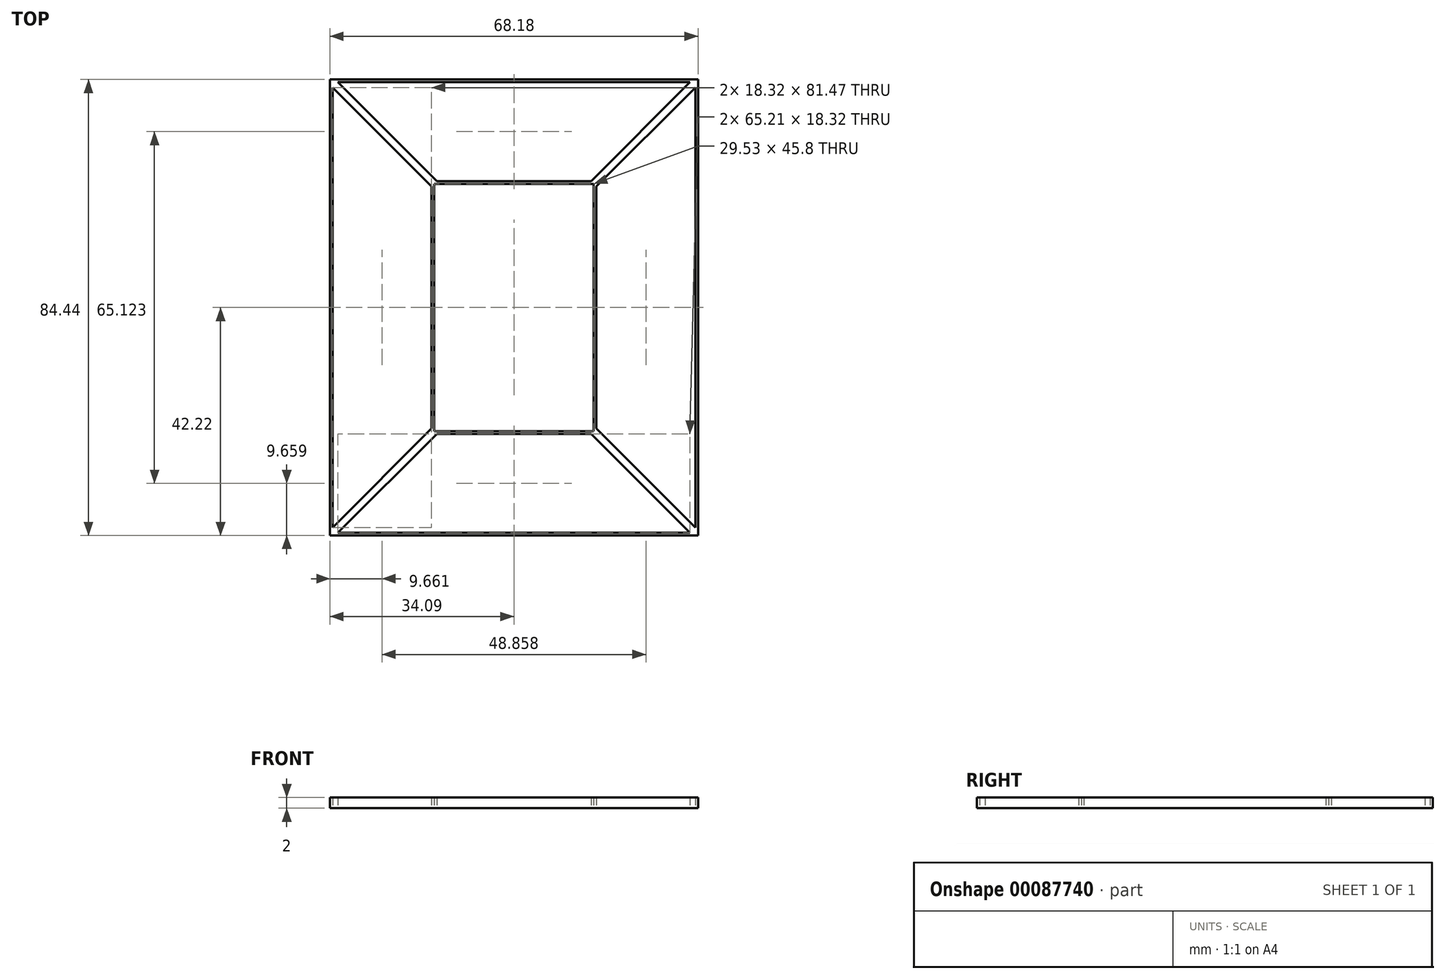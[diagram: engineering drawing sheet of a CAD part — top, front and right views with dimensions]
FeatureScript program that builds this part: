
annotation { "Feature Type Name" : "Feature", "Feature Type Description" : "" }
export const myFeature = defineFeature(function(context is Context, id is Id, definition is map)
    precondition{}
    {
        {
            var Q0;
            Q0=qCreatedBy(makeId("Top.planeOp"),FACE);
            var sketch = newSketch(context, id + "F0", { "sketchPlane" : qUnion([Q0])});
            skLineSegment(sketch, "E0", {"start": v(-33.6, 41.72) * mm, "end": v(-33.6, -41.72) * mm});
            skLineSegment(sketch, "E1", {"start": v(-33.6, -41.72) * mm, "end": v(33.6, -41.72) * mm});
            skLineSegment(sketch, "E2", {"start": v(33.6, -41.72) * mm, "end": v(33.6, 41.72) * mm});
            skLineSegment(sketch, "E3", {"start": v(33.6, 41.72) * mm, "end": v(-33.6, 41.72) * mm});
            skLineSegment(sketch, "E4.0", {"start": v(34.1, 42.22) * mm, "end": v(-34.1, 42.22) * mm});
            skLineSegment(sketch, "E4.1", {"start": v(34.1, -42.22) * mm, "end": v(34.1, 42.22) * mm});
            skLineSegment(sketch, "E4.2", {"start": v(-34.1, -42.22) * mm, "end": v(34.1, -42.22) * mm});
            skLineSegment(sketch, "E4.3", {"start": v(-34.1, 42.22) * mm, "end": v(-34.1, -42.22) * mm});
            skLineSegment(sketch, "E5.bottom", {"start": v(-14.77, 22.9) * mm, "end": v(14.77, 22.9) * mm});
            skLineSegment(sketch, "E5.top", {"start": v(-14.77, -22.9) * mm, "end": v(14.77, -22.9) * mm});
            skLineSegment(sketch, "E5.left", {"start": v(-14.77, 22.9) * mm, "end": v(-14.77, -22.9) * mm});
            skLineSegment(sketch, "E5.right", {"start": v(14.77, 22.9) * mm, "end": v(14.77, -22.9) * mm});
            skLineSegment(sketch, "E6.0", {"start": v(-15.27, 23.4) * mm, "end": v(15.27, 23.4) * mm});
            skLineSegment(sketch, "E6.1", {"start": v(-15.27, 23.4) * mm, "end": v(-15.27, -23.4) * mm});
            skLineSegment(sketch, "E6.2", {"start": v(-15.27, -23.4) * mm, "end": v(15.27, -23.4) * mm});
            skLineSegment(sketch, "E6.3", {"start": v(15.27, 23.4) * mm, "end": v(15.27, -23.4) * mm});
            skLineSegment(sketch, "E7", {"start": v(-32.6, -41.72) * mm, "end": v(-14.28, -23.4) * mm});
            skLineSegment(sketch, "E8", {"start": v(-33.6, -41.72) * mm, "end": v(-15.27, -23.4) * mm, "construction": true});
            skLineSegment(sketch, "E9.MirrorCS", {"start": v(-33.6, -40.74) * mm, "end": v(-15.27, -22.41) * mm});
            skLineSegment(sketch, "E10", {"start": v(0, -42.22) * mm, "end": v(0, 34.98) * mm, "construction": true});
            skLineSegment(sketch, "E11", {"start": v(-33.6, 0) * mm, "end": v(33.6, 0) * mm, "construction": true});
            skLineSegment(sketch, "E12.MirrorCS", {"start": v(-33.6, 40.74) * mm, "end": v(-15.27, 22.41) * mm});
            skLineSegment(sketch, "E13.MirrorCS", {"start": v(-32.6, 41.72) * mm, "end": v(-14.28, 23.4) * mm});
            skLineSegment(sketch, "E14.MirrorCS", {"start": v(33.6, 40.74) * mm, "end": v(15.27, 22.41) * mm});
            skLineSegment(sketch, "E15.MirrorCS", {"start": v(32.6, 41.72) * mm, "end": v(14.28, 23.4) * mm});
            skLineSegment(sketch, "E16.MirrorCS", {"start": v(33.6, -40.74) * mm, "end": v(15.27, -22.41) * mm});
            skLineSegment(sketch, "E17.MirrorCS", {"start": v(32.6, -41.72) * mm, "end": v(14.28, -23.4) * mm});
            skSolve(sketch);
        }
        {
            var Q0;
            Q0=makeQuery(id+"F0.imprint","IMPRINT",FACE,{"disambiguationData":[TD([[makeQuery(id+"F0.imprint","IMPRINT",EDGE,{"derivedFrom":sQuery(id+"F0.wireOp",EDGE,"E4.0")}),1.0]])]});
            var Q1;
            {var subQ3=sQuery(id+"F0.wireOp",EDGE,"E7");Q1=makeQuery(id+"F0.imprint","IMPRINT",FACE,{"disambiguationData":[TD([[makeQuery(id+"F0.imprint","IMPRINT",EDGE,{"derivedFrom":subQ3}),1.0]])]});}
            var Q2;
            {var subQ7=sQuery(id+"F0.wireOp",EDGE,"E12.MirrorCS");Q2=makeQuery(id+"F0.imprint","IMPRINT",FACE,{"disambiguationData":[TD([[makeQuery(id+"F0.imprint","IMPRINT",EDGE,{"derivedFrom":subQ7}),1.0]])]});}
            var Q3;
            {var subQ3=sQuery(id+"F0.wireOp",EDGE,"E14.MirrorCS");Q3=makeQuery(id+"F0.imprint","IMPRINT",FACE,{"disambiguationData":[TD([[makeQuery(id+"F0.imprint","IMPRINT",EDGE,{"derivedFrom":subQ3}),-1.0]])]});}
            var Q4;
            {var subQ3=sQuery(id+"F0.wireOp",EDGE,"E16.MirrorCS");Q4=makeQuery(id+"F0.imprint","IMPRINT",FACE,{"disambiguationData":[TD([[makeQuery(id+"F0.imprint","IMPRINT",EDGE,{"derivedFrom":subQ3}),1.0]])]});}
            var Q5;
            Q5=makeQuery(id+"F0.imprint","IMPRINT",FACE,{"disambiguationData":[TD([[makeQuery(id+"F0.imprint","IMPRINT",EDGE,{"derivedFrom":sQuery(id+"F0.wireOp",EDGE,"E5.bottom")}),1.0]])]});
            extrude(context, id + "F1", {"entities" : qUnion([Q0, Q1, Q2, Q3, Q4, Q5]), "depth" : 2 * mm});
        }
    });
